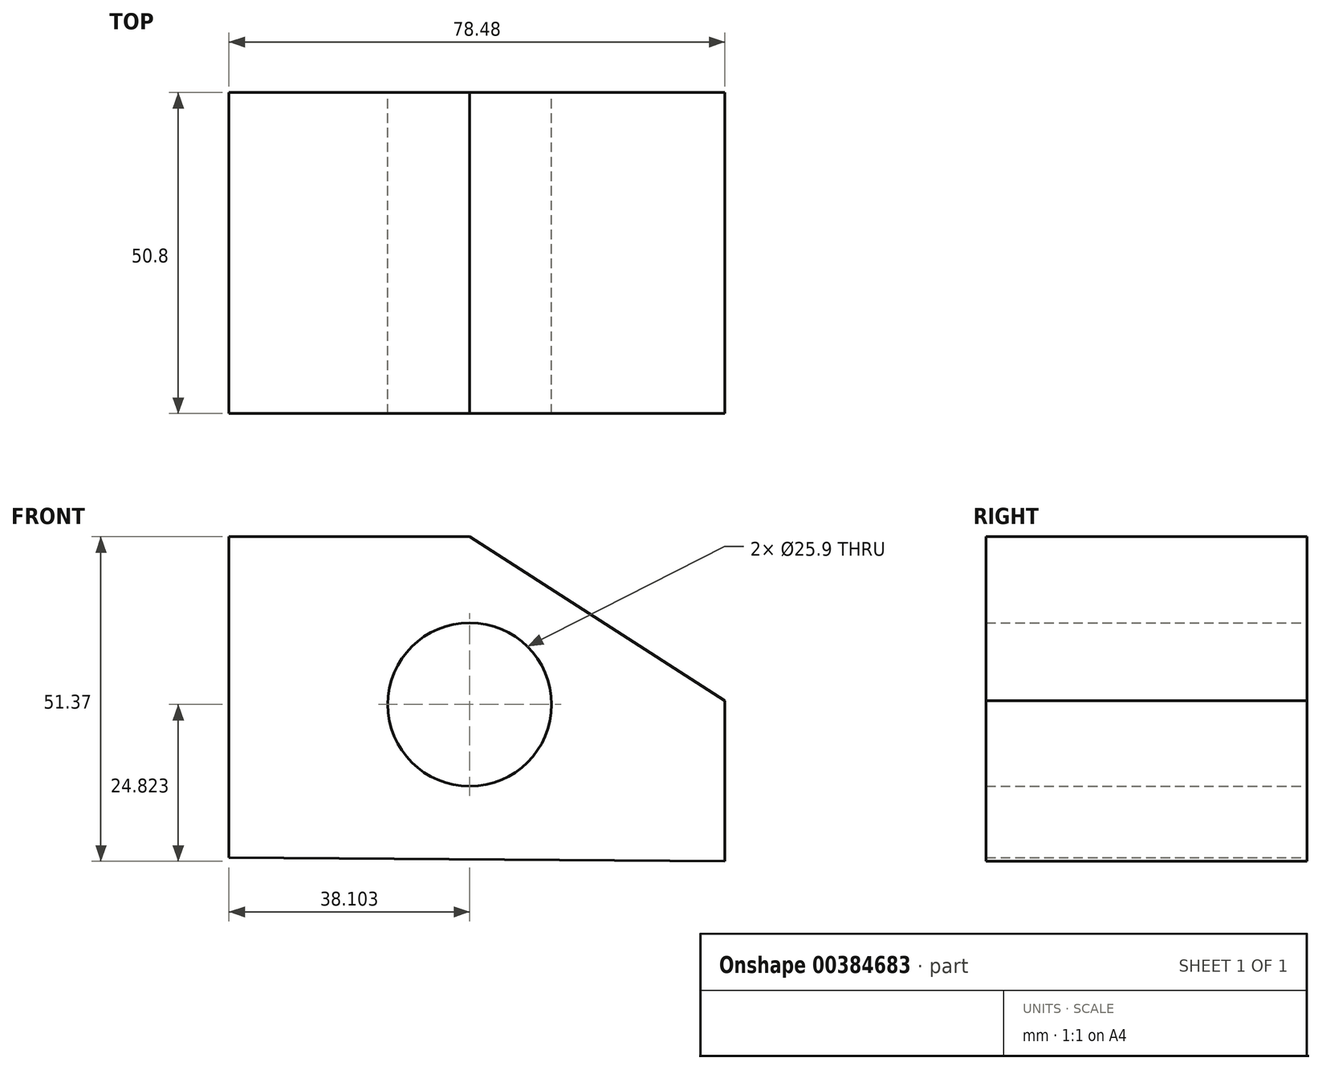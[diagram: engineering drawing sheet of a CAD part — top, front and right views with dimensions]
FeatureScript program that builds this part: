
annotation { "Feature Type Name" : "Feature", "Feature Type Description" : "" }
export const myFeature = defineFeature(function(context is Context, id is Id, definition is map)
    precondition{}
    {
        {
            var Q0;
            Q0=qCreatedBy(makeId("Front.planeOp"),FACE);
            var sketch = newSketch(context, id + "F0", { "sketchPlane" : qUnion([Q0])});
            skLineSegment(sketch, "E0", {"start": v(-81.26, 22.23) * mm, "end": v(-81.26, -28.57) * mm});
            skLineSegment(sketch, "E1", {"start": v(-43.16, 22.23) * mm, "end": v(-81.26, 22.23) * mm});
            skLineSegment(sketch, "E2", {"start": v(-43.16, 22.23) * mm, "end": v(-2.78, -3.74) * mm});
            skLineSegment(sketch, "E3", {"start": v(-2.78, -29.14) * mm, "end": v(-2.78, -3.74) * mm});
            skLineSegment(sketch, "E4", {"start": v(-81.26, -28.57) * mm, "end": v(-2.78, -29.14) * mm});
            skCircle(sketch, "E5", {"center": v(-43.16, -4.32) * mm, "radius": 12.95 * mm});
            skSolve(sketch);
        }
        {
            var Q0;
            Q0 = qSketchRegion(id + "F0", true);
            extrude(context, id + "F1", {"entities" : qUnion([Q0]), "depth" : 50.8 * mm});
        }
    });
